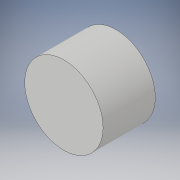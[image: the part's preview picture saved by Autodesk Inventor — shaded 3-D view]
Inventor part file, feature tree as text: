
AUTODESK INVENTOR PART (.ipt)
format: ipt  version: 2019 (Build 230136000, 136)  size: 92,672 bytes
history: native  units: mm
features: extrude x1, sketch x1
ambient origin geometry x8: Origin, YZ Plane, XZ Plane, XY Plane, X Axis, Y Axis, Z Axis, Center Point
bodies: Solid1 (feature_tree)
feature tree (2):
  extrude  "Extrusion1"  Depth=10.0mm TaperAngle=0.0deg
  sketch  "Sketch1"  dims[d0=15.0mm d1=10.0mm d2=0.0mm]
